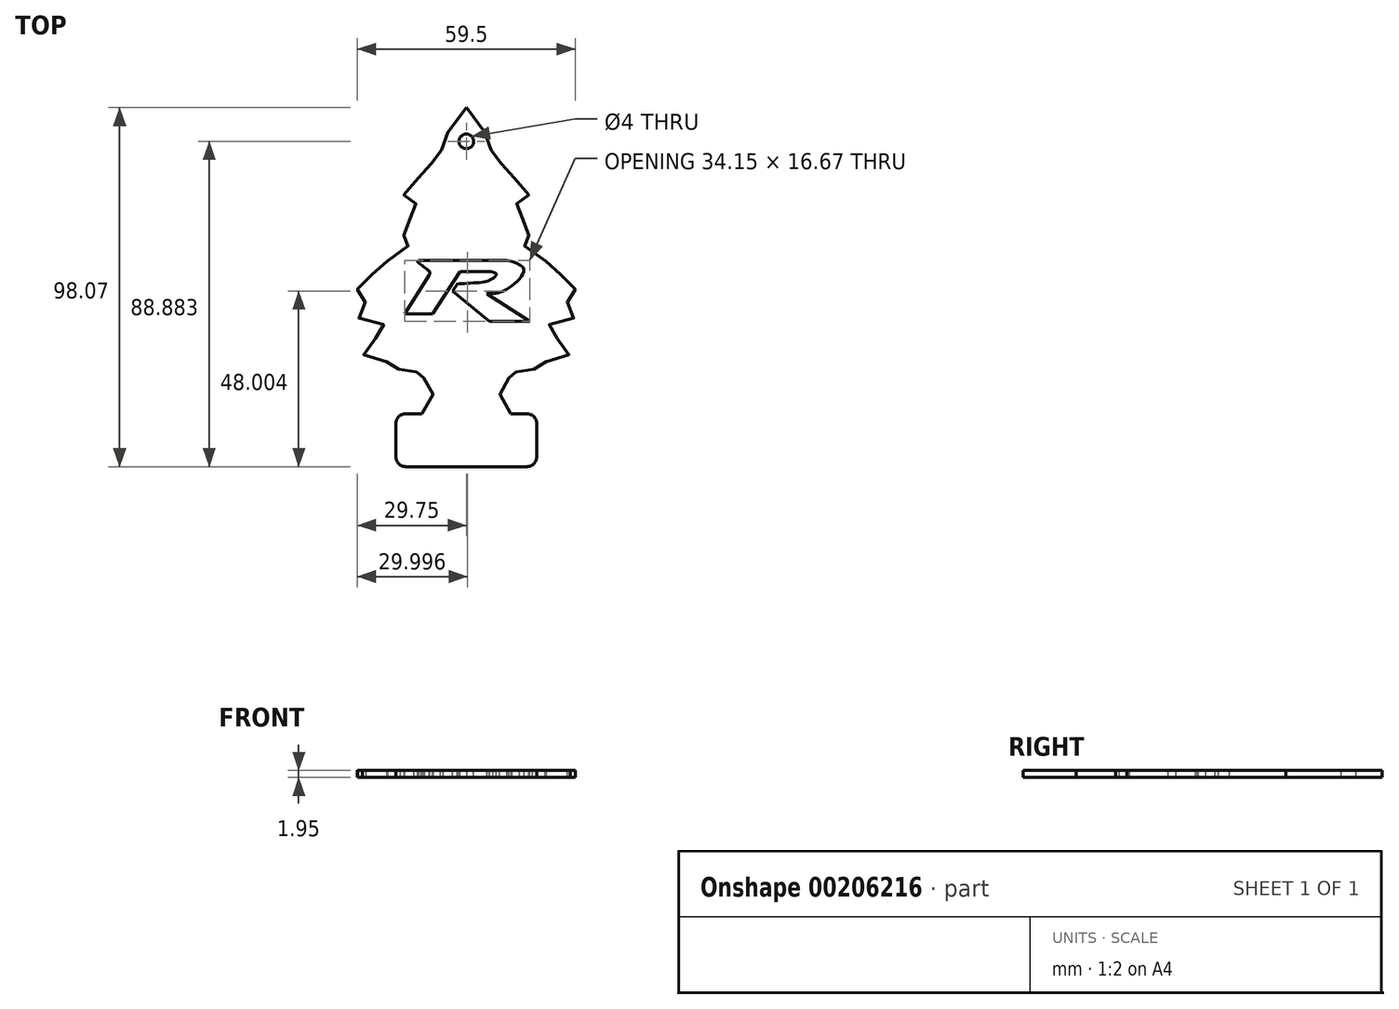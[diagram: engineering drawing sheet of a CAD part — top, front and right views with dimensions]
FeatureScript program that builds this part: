
annotation { "Feature Type Name" : "Feature", "Feature Type Description" : "" }
export const myFeature = defineFeature(function(context is Context, id is Id, definition is map)
    precondition{}
    {
        {
            var Q0;
            Q0=qCreatedBy(makeId("Top.planeOp"),FACE);
            var sketch = newSketch(context, id + "F0", { "sketchPlane" : qUnion([Q0])});
            skLineSegment(sketch, "E0", {"start": v(0, -59.88) * mm, "end": v(0, 68.26) * mm, "construction": true});
            skFitSpline(sketch, "E1", {"points": [v(0, 45.5) * mm, v(2.33, 41.7) * mm, v(4.5, 39.78) * mm, v(5.5, 37.8) * mm, v(5.41, 36.75) * mm, v(4.92, 36.1) * mm, v(5.65, 35.25) * mm, v(7.35, 33.76) * mm, v(8, 32) * mm, v(8.56, 31.35) * mm, v(11.1, 30.1) * mm, v(12.7, 28.27) * mm, v(13.12, 27.2) * mm, v(13, 25.6) * mm, v(12, 25.25) * mm, v(10.19, 25.25) * mm, v(9.69, 24.88) * mm, v(9.71, 24.1) * mm, v(13.3, 21.06) * mm, v(13.9, 19.85) * mm, v(13.33, 18.86) * mm, v(11.34, 17.68) * mm, v(11.16, 17.23) * mm, v(11.81, 16.65) * mm, v(15.71, 14.67) * mm, v(16.7, 13.6) * mm, v(16.6, 11.87) * mm, v(17.15, 11.52) * mm, v(20.74, 9.94) * mm, v(22.12, 8.78) * mm, v(22.82, 7.74) * mm, v(22.7, 6.5) * mm, v(21.83, 5.83) * mm, v(21.2, 4.92) * mm, v(21.43, 4.35) * mm, v(22.52, 3.3) * mm, v(22.77, 1.72) * mm, v(21.08, 0.31) * mm, v(17.86, 0) * mm, v(16.9, -0.5) * mm, v(16.93, -1.3) * mm, v(18.81, -2.8) * mm, v(21.55, -4.57) * mm, v(21.82, -5.76) * mm, v(20.88, -7.15) * mm, v(18.1, -8.15) * mm, v(15.88, -7.65) * mm, v(15.24, -7.62) * mm, v(14.74, -8.74) * mm, v(13.55, -9.9) * mm, v(12.03, -10.42) * mm, v(10.78, -10.24) * mm, v(9.64, -9.75) * mm, v(9.13, -9.84) * mm, v(8.83, -10.4) * mm, v(8.91, -11.33) * mm, v(8.32, -12.22) * mm, v(7.2, -13.3) * mm, v(7.2, -15.5) * mm, v(8.33, -17.52) * mm, v(9.33, -18.83) * mm], "startDerivative": vector(76.66, -152.99) * mm, "endDerivative": vector(54.27, -70.02) * mm});
            skLineSegment(sketch, "E2", {"start": v(9.33, -18.83) * mm, "end": v(12.78, -18.83) * mm});
            skLineSegment(sketch, "E3", {"start": v(14.78, -20.83) * mm, "end": v(14.78, -27.93) * mm});
            skLineSegment(sketch, "E4", {"start": v(12.78, -29.93) * mm, "end": v(0, -29.93) * mm});
            skPoint(sketch, "E5.visualSharp", {"position": v(14.78, -18.83) * mm});
            skArc(sketch, "E5.filletArc", {"start": v(14.78, -20.83) * mm, "mid": v(14.2, -19.42) * mm, "end": v(12.78, -18.83) * mm});
            skPoint(sketch, "E6.visualSharp", {"position": v(14.78, -29.93) * mm});
            skArc(sketch, "E6.filletArc", {"start": v(12.78, -29.93) * mm, "mid": v(14.2, -29.34) * mm, "end": v(14.78, -27.93) * mm});
            skArc(sketch, "E7.MirrorCS", {"start": v(-12.78, -29.93) * mm, "mid": v(-14.2, -29.34) * mm, "end": v(-14.78, -27.93) * mm});
            skArc(sketch, "E8.MirrorCS", {"start": v(-14.78, -20.83) * mm, "mid": v(-14.2, -19.42) * mm, "end": v(-12.78, -18.83) * mm});
            skLineSegment(sketch, "E9.MirrorCS", {"start": v(-9.33, -18.83) * mm, "end": v(-12.78, -18.83) * mm});
            skPoint(sketch, "E10.MirrorP", {"position": v(-14.78, -29.93) * mm});
            skPoint(sketch, "E11.MirrorP", {"position": v(-14.78, -18.83) * mm});
            skLineSegment(sketch, "E12.MirrorCS", {"start": v(-12.78, -29.93) * mm, "end": v(0, -29.93) * mm});
            skFitSpline(sketch, "E13.MirrorCS", {"points": [v(0, 45.5) * mm, v(-2.33, 41.7) * mm, v(-4.5, 39.78) * mm, v(-5.5, 37.8) * mm, v(-5.41, 36.75) * mm, v(-4.92, 36.1) * mm, v(-5.65, 35.25) * mm, v(-7.35, 33.76) * mm, v(-8, 32) * mm, v(-8.56, 31.35) * mm, v(-11.1, 30.1) * mm, v(-12.7, 28.27) * mm, v(-13.12, 27.2) * mm, v(-13, 25.6) * mm, v(-12, 25.25) * mm, v(-10.19, 25.25) * mm, v(-9.69, 24.88) * mm, v(-9.71, 24.1) * mm, v(-13.3, 21.06) * mm, v(-13.9, 19.85) * mm, v(-13.33, 18.86) * mm, v(-11.34, 17.68) * mm, v(-11.16, 17.23) * mm, v(-11.81, 16.65) * mm, v(-15.71, 14.67) * mm, v(-16.7, 13.6) * mm, v(-16.6, 11.87) * mm, v(-17.15, 11.52) * mm, v(-20.74, 9.94) * mm, v(-22.12, 8.78) * mm, v(-22.82, 7.74) * mm, v(-22.7, 6.5) * mm, v(-21.83, 5.83) * mm, v(-21.2, 4.92) * mm, v(-21.43, 4.35) * mm, v(-22.52, 3.3) * mm, v(-22.77, 1.72) * mm, v(-21.08, 0.31) * mm, v(-17.86, 0) * mm, v(-16.9, -0.5) * mm, v(-16.93, -1.3) * mm, v(-18.81, -2.8) * mm, v(-21.55, -4.57) * mm, v(-21.82, -5.76) * mm, v(-20.88, -7.15) * mm, v(-18.1, -8.15) * mm, v(-15.88, -7.65) * mm, v(-15.24, -7.62) * mm, v(-14.74, -8.74) * mm, v(-13.55, -9.9) * mm, v(-12.03, -10.42) * mm, v(-10.78, -10.24) * mm, v(-9.64, -9.75) * mm, v(-9.13, -9.84) * mm, v(-8.83, -10.4) * mm, v(-8.91, -11.33) * mm, v(-8.32, -12.22) * mm, v(-7.2, -13.3) * mm, v(-7.2, -15.5) * mm, v(-8.33, -17.52) * mm, v(-9.33, -18.83) * mm], "startDerivative": vector(-76.66, -152.99) * mm, "endDerivative": vector(-54.27, -70.02) * mm});
            skLineSegment(sketch, "E14.MirrorCS", {"start": v(-14.78, -20.83) * mm, "end": v(-14.78, -27.93) * mm});
            skSolve(sketch);
        }
        {
            var Q0;
            Q0 = qSketchRegion(id + "F0", true);
            extrude(context, id + "F1", {"entities" : qUnion([Q0]), "depth" : 1.5 * mm});
        }
        {
            var Q0;
            Q0=makeQuery(id+"F1.opExtrude","SWEPT_BODY",BODY,{"disambiguationData":[OSD([sQuery(id+"F0.wireOp",EDGE,"E1"),sQuery(id+"F0.wireOp",EDGE,"E2"),sQuery(id+"F0.wireOp",EDGE,"E3"),sQuery(id+"F0.wireOp",EDGE,"E4"),sQuery(id+"F0.wireOp",EDGE,"E5.filletArc"),sQuery(id+"F0.wireOp",EDGE,"E6.filletArc"),sQuery(id+"F0.wireOp",EDGE,"E7.MirrorCS"),sQuery(id+"F0.wireOp",EDGE,"E8.MirrorCS"),sQuery(id+"F0.wireOp",EDGE,"E9.MirrorCS"),sQuery(id+"F0.wireOp",EDGE,"E12.MirrorCS"),sQuery(id+"F0.wireOp",EDGE,"E13.MirrorCS"),sQuery(id+"F0.wireOp",EDGE,"E14.MirrorCS")])]});
            var Q1;
            Q1=qCreatedBy(makeId("Origin.pointOp"),VERTEX);
            transform(context, id + "F2", {"entities" : qUnion([Q0]), "transformType" : TransformType.SCALE_UNIFORMLY, "scale" : 1.3, "scalePoint" : qUnion([Q1]), "makeCopy" : false});
        }
        {
            var Q0;
            Q0=makeQuery(id+"F1.opExtrude","CAP_FACE",FACE,{"disambiguationData":[OSD([sQuery(id+"F0.wireOp",EDGE,"E1"),sQuery(id+"F0.wireOp",EDGE,"E2"),sQuery(id+"F0.wireOp",EDGE,"E3"),sQuery(id+"F0.wireOp",EDGE,"E4"),sQuery(id+"F0.wireOp",EDGE,"E5.filletArc"),sQuery(id+"F0.wireOp",EDGE,"E6.filletArc"),sQuery(id+"F0.wireOp",EDGE,"E7.MirrorCS"),sQuery(id+"F0.wireOp",EDGE,"E8.MirrorCS"),sQuery(id+"F0.wireOp",EDGE,"E9.MirrorCS"),sQuery(id+"F0.wireOp",EDGE,"E12.MirrorCS"),sQuery(id+"F0.wireOp",EDGE,"E13.MirrorCS"),sQuery(id+"F0.wireOp",EDGE,"E14.MirrorCS")])],"isStart":false});
            var sketch = newSketch(context, id + "F3", { "sketchPlane" : qUnion([Q0])});
            skCircle(sketch, "E15", {"center": v(0, 49.97) * mm, "radius": 2 * mm});
            skSolve(sketch);
        }
        {
            var Q0;
            Q0 = qSketchRegion(id + "F3", true);
            extrude(context, id + "F4", {"entities" : qUnion([Q0]), "operationType" : NewBodyOperationType.REMOVE, "endBound" : BoundingType.THROUGH_ALL, "oppositeDirection" : true, "depth" : 25 * mm});
        }
        {
            var Q0;
            Q0=makeQuery(id+"F1.opExtrude","CAP_FACE",FACE,{"disambiguationData":[OSD([sQuery(id+"F0.wireOp",EDGE,"E1"),sQuery(id+"F0.wireOp",EDGE,"E2"),sQuery(id+"F0.wireOp",EDGE,"E3"),sQuery(id+"F0.wireOp",EDGE,"E4"),sQuery(id+"F0.wireOp",EDGE,"E5.filletArc"),sQuery(id+"F0.wireOp",EDGE,"E6.filletArc"),sQuery(id+"F0.wireOp",EDGE,"E7.MirrorCS"),sQuery(id+"F0.wireOp",EDGE,"E8.MirrorCS"),sQuery(id+"F0.wireOp",EDGE,"E9.MirrorCS"),sQuery(id+"F0.wireOp",EDGE,"E12.MirrorCS"),sQuery(id+"F0.wireOp",EDGE,"E13.MirrorCS"),sQuery(id+"F0.wireOp",EDGE,"E14.MirrorCS")])],"isStart":false});
            var sketch = newSketch(context, id + "F5", { "sketchPlane" : qUnion([Q0])});
            skLineSegment(sketch, "E16", {"start": v(-12.86, 17.43) * mm, "end": v(11.06, 17.43) * mm});
            skLineSegment(sketch, "E17", {"start": v(-1.78, 14.38) * mm, "end": v(-9.25, 2.88) * mm});
            skLineSegment(sketch, "E18", {"start": v(-9.25, 2.88) * mm, "end": v(-16.83, 2.88) * mm});
            skLineSegment(sketch, "E19", {"start": v(-16.83, 2.88) * mm, "end": v(-10.05, 13.49) * mm});
            skLineSegment(sketch, "E20", {"start": v(5.66, 8.22) * mm, "end": v(17.32, 0.76) * mm});
            skLineSegment(sketch, "E21", {"start": v(17.32, 0.76) * mm, "end": v(6.32, 0.76) * mm});
            skLineSegment(sketch, "E22", {"start": v(6.32, 0.76) * mm, "end": v(-3.75, 8.98) * mm});
            skLineSegment(sketch, "E23", {"start": v(-3.75, 8.98) * mm, "end": v(-2.45, 10.96) * mm});
            skFitSpline(sketch, "E24", {"points": [v(11.06, 17.43) * mm, v(13.04, 16.95) * mm, v(15.32, 15.68) * mm, v(15.78, 14.62) * mm, v(15.33, 13.55) * mm, v(14.14, 11.98) * mm, v(12.4, 10.48) * mm, v(10.5, 9.2) * mm, v(8.94, 8.64) * mm, v(7.37, 8.38) * mm, v(5.97, 8.5) * mm, v(5.75, 8.44) * mm, v(5.66, 8.22) * mm], "startDerivative": vector(19.05, -3.43) * mm, "endDerivative": vector(0.21, -10.76) * mm});
            skFitSpline(sketch, "E25", {"points": [v(-2.45, 10.96) * mm, v(-0.92, 11.05) * mm, v(1.5, 11.24) * mm, v(3.89, 11.42) * mm, v(5.52, 11.68) * mm, v(6.43, 12.05) * mm, v(7.4, 12.64) * mm, v(8.16, 13.46) * mm, v(8.14, 13.81) * mm, v(7.73, 14.12) * mm, v(7.08, 14.3) * mm, v(6.24, 14.37) * mm], "startDerivative": vector(16.27, 2.13) * mm, "endDerivative": vector(-13.09, -0.05) * mm});
            skLineSegment(sketch, "E26", {"start": v(6.24, 14.37) * mm, "end": v(-1.78, 14.38) * mm});
            skFitSpline(sketch, "E27", {"points": [v(-10.05, 13.49) * mm, v(-9.95, 14.07) * mm, v(-10.26, 14.6) * mm, v(-13.26, 16.95) * mm, v(-13.27, 17.08) * mm, v(-12.86, 17.43) * mm], "startDerivative": vector(1.5, 3.76) * mm, "endDerivative": vector(4.88, 0.36) * mm});
            skSolve(sketch);
        }
        {
            var Q0;
            Q0 = qSketchRegion(id + "F5", true);
            extrude(context, id + "F6", {"entities" : qUnion([Q0]), "operationType" : NewBodyOperationType.REMOVE, "endBound" : BoundingType.THROUGH_ALL, "oppositeDirection" : true, "depth" : 25 * mm});
        }
    });
